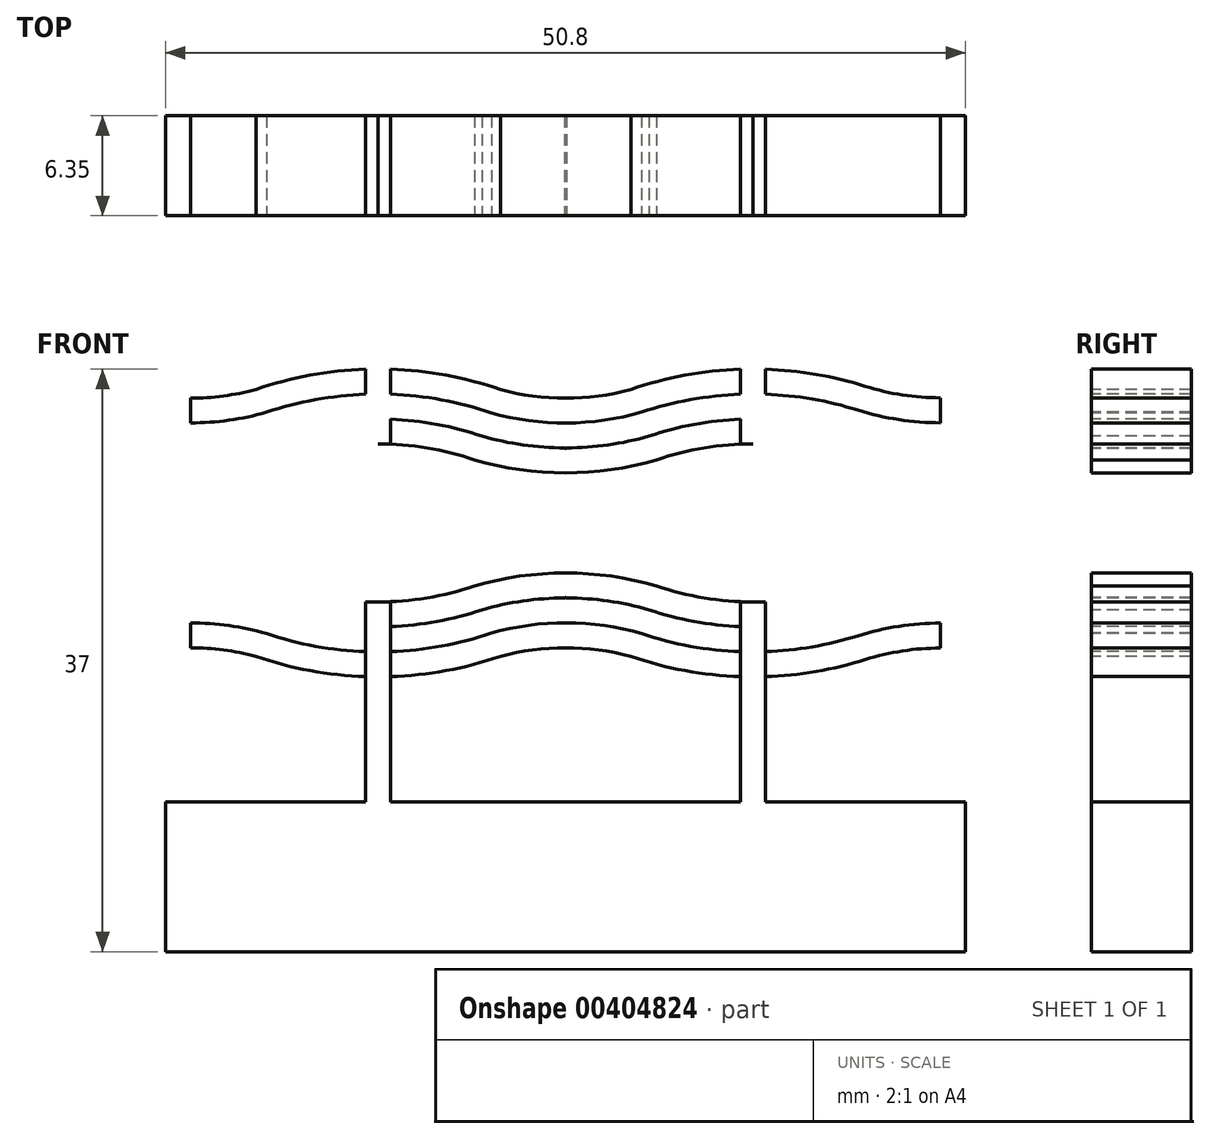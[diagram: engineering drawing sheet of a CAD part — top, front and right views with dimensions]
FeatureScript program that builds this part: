
annotation { "Feature Type Name" : "Feature", "Feature Type Description" : "" }
export const myFeature = defineFeature(function(context is Context, id is Id, definition is map)
    precondition{}
    {
        {
            var Q0;
            Q0=qCreatedBy(makeId("Front.planeOp"),FACE);
            var sketch = newSketch(context, id + "F0", { "sketchPlane" : qUnion([Q0])});
            skLineSegment(sketch, "E0.bottom", {"start": v(25.4, -4.76) * mm, "end": v(-25.4, -4.76) * mm});
            skLineSegment(sketch, "E0.top", {"start": v(25.4, 4.76) * mm, "end": v(-25.4, 4.76) * mm});
            skLineSegment(sketch, "E0.left", {"start": v(25.4, -4.76) * mm, "end": v(25.4, 4.76) * mm});
            skLineSegment(sketch, "E0.right", {"start": v(-25.4, -4.76) * mm, "end": v(-25.4, 4.76) * mm});
            skPoint(sketch, "E0.middle", {"position": v(0, 0) * mm});
            skLineSegment(sketch, "E1.bottom", {"start": v(-12.7, 4.76) * mm, "end": v(-11.11, 4.76) * mm});
            skLineSegment(sketch, "E1.top", {"start": v(-12.7, 17.46) * mm, "end": v(-11.11, 17.46) * mm});
            skLineSegment(sketch, "E1.left", {"start": v(-12.7, 4.76) * mm, "end": v(-12.7, 17.46) * mm});
            skLineSegment(sketch, "E1.right", {"start": v(-11.11, 4.76) * mm, "end": v(-11.11, 17.46) * mm});
            skLineSegment(sketch, "E2.bottom", {"start": v(11.11, 17.46) * mm, "end": v(12.7, 17.46) * mm});
            skLineSegment(sketch, "E2.top", {"start": v(11.11, 4.76) * mm, "end": v(12.7, 4.76) * mm});
            skLineSegment(sketch, "E2.left", {"start": v(12.7, 17.46) * mm, "end": v(12.7, 4.76) * mm});
            skLineSegment(sketch, "E2.right", {"start": v(11.11, 17.46) * mm, "end": v(11.11, 4.76) * mm});
            skSolve(sketch);
        }
        {
            var Q0;
            Q0 = qSketchRegion(id + "F0", true);
            extrude(context, id + "F1", {"entities" : qUnion([Q0]), "depth" : 6.35 * mm});
        }
        {
            var Q0;
            Q0=makeQuery(id+"F1.opExtrude","CAP_FACE",FACE,{"disambiguationData":[OSD([sQuery(id+"F0.wireOp",EDGE,"E0.bottom"),sQuery(id+"F0.wireOp",EDGE,"E0.top"),sQuery(id+"F0.wireOp",EDGE,"E0.left"),sQuery(id+"F0.wireOp",EDGE,"E0.right"),sQuery(id+"F0.wireOp",EDGE,"E1.top"),sQuery(id+"F0.wireOp",EDGE,"E1.left"),sQuery(id+"F0.wireOp",EDGE,"E1.right"),sQuery(id+"F0.wireOp",EDGE,"E2.bottom"),sQuery(id+"F0.wireOp",EDGE,"E2.left"),sQuery(id+"F0.wireOp",EDGE,"E2.right")])],"isStart":false});
            var sketch = newSketch(context, id + "F2", { "sketchPlane" : qUnion([Q0])});
            skArc(sketch, "E3", {"start": v(-18.03, 18.47) * mm, "mid": v(-11.9, 17.46) * mm, "end": v(-5.78, 18.47) * mm});
            skLineSegment(sketch, "E4", {"start": v(-11.9, 17.46) * mm, "end": v(-11.9, -4.76) * mm, "construction": true});
            skLineSegment(sketch, "E5", {"start": v(11.9, 17.46) * mm, "end": v(11.9, -4.76) * mm, "construction": true});
            skArc(sketch, "E6", {"start": v(5.78, 18.47) * mm, "mid": v(11.9, 17.46) * mm, "end": v(18.03, 18.47) * mm});
            skArc(sketch, "E7", {"start": v(-18.51, 16.96) * mm, "mid": v(-11.9, 15.88) * mm, "end": v(-5.3, 16.96) * mm});
            skArc(sketch, "E8", {"start": v(5.3, 16.96) * mm, "mid": v(11.9, 15.88) * mm, "end": v(18.51, 16.96) * mm});
            skArc(sketch, "E9", {"start": v(5.3, 16.96) * mm, "mid": v(0, 17.71) * mm, "end": v(-5.3, 16.96) * mm});
            skArc(sketch, "E10.trimOffspring", {"start": v(5.78, 18.47) * mm, "mid": v(0, 19.3) * mm, "end": v(-5.78, 18.47) * mm});
            skArc(sketch, "E11.MirrorCS", {"start": v(-23.81, 19.3) * mm, "mid": v(-20.9, 19.1) * mm, "end": v(-18.03, 18.47) * mm});
            skArc(sketch, "E12.MirrorCS", {"start": v(-23.81, 17.71) * mm, "mid": v(-21.13, 17.52) * mm, "end": v(-18.51, 16.96) * mm});
            skArc(sketch, "E13.MirrorCS", {"start": v(18.03, 18.47) * mm, "mid": v(20.9, 19.1) * mm, "end": v(23.81, 19.3) * mm});
            skArc(sketch, "E14.MirrorCS", {"start": v(18.51, 16.96) * mm, "mid": v(21.13, 17.52) * mm, "end": v(23.81, 17.71) * mm});
            skLineSegment(sketch, "E15", {"start": v(-23.81, 19.3) * mm, "end": v(-23.81, 17.71) * mm});
            skLineSegment(sketch, "E16", {"start": v(23.81, 19.3) * mm, "end": v(23.81, 17.71) * mm});
            skPoint(sketch, "E16.startSnap0", {"position": v(23.81, 19.3) * mm});
            skLineSegment(sketch, "E17", {"start": v(-25.4, 22.48) * mm, "end": v(25.4, 22.48) * mm, "construction": true});
            skArc(sketch, "E18.MirrorCS", {"start": v(-23.81, 25.65) * mm, "mid": v(-20.9, 25.86) * mm, "end": v(-18.03, 26.48) * mm});
            skArc(sketch, "E19.MirrorCS", {"start": v(-23.81, 27.24) * mm, "mid": v(-21.13, 27.43) * mm, "end": v(-18.51, 28) * mm});
            skArc(sketch, "E20.MirrorCS", {"start": v(-18.51, 28) * mm, "mid": v(-11.9, 29.08) * mm, "end": v(-5.3, 28) * mm});
            skArc(sketch, "E21.MirrorCS", {"start": v(-18.03, 26.48) * mm, "mid": v(-11.9, 27.49) * mm, "end": v(-5.78, 26.48) * mm});
            skArc(sketch, "E22.MirrorCS", {"start": v(5.78, 26.48) * mm, "mid": v(0, 25.65) * mm, "end": v(-5.78, 26.48) * mm});
            skArc(sketch, "E23.MirrorCS", {"start": v(5.3, 28) * mm, "mid": v(0, 27.24) * mm, "end": v(-5.3, 28) * mm});
            skArc(sketch, "E24.MirrorCS", {"start": v(5.78, 26.48) * mm, "mid": v(11.9, 27.49) * mm, "end": v(18.03, 26.48) * mm});
            skArc(sketch, "E25.MirrorCS", {"start": v(5.3, 28) * mm, "mid": v(11.9, 29.08) * mm, "end": v(18.51, 28) * mm});
            skArc(sketch, "E26.MirrorCS", {"start": v(18.03, 26.48) * mm, "mid": v(20.9, 25.86) * mm, "end": v(23.81, 25.65) * mm});
            skArc(sketch, "E27.MirrorCS", {"start": v(18.51, 28) * mm, "mid": v(21.13, 27.43) * mm, "end": v(23.81, 27.24) * mm});
            skLineSegment(sketch, "E28.MirrorCS", {"start": v(23.81, 25.65) * mm, "end": v(23.81, 27.24) * mm});
            skLineSegment(sketch, "E29", {"start": v(-23.81, 27.24) * mm, "end": v(-23.81, 25.65) * mm});
            skArc(sketch, "E30", {"start": v(-18.98, 15.44) * mm, "mid": v(-21.37, 15.95) * mm, "end": v(-23.81, 16.13) * mm});
            skArc(sketch, "E31", {"start": v(-23.81, 17.75) * mm, "mid": v(-23.79, 17.73) * mm, "end": v(-23.76, 17.71) * mm});
            skArc(sketch, "E32", {"start": v(0, 17.75) * mm, "mid": v(0.03, 17.73) * mm, "end": v(0.05, 17.71) * mm});
            skArc(sketch, "E33", {"start": v(23.81, 16.12) * mm, "mid": v(21.16, 15.91) * mm, "end": v(18.58, 15.31) * mm});
            skArc(sketch, "E34.trimOffspring", {"start": v(-18.98, 15.44) * mm, "mid": v(-11.84, 14.29) * mm, "end": v(-4.7, 15.49) * mm});
            skArc(sketch, "E35.trimOffspring", {"start": v(-0.05, 17.71) * mm, "mid": v(-0.03, 17.73) * mm, "end": v(0, 17.75) * mm});
            skArc(sketch, "E36.trimOffspring", {"start": v(4.83, 15.44) * mm, "mid": v(11.7, 14.29) * mm, "end": v(18.58, 15.31) * mm});
            skArc(sketch, "E37.trimOffspring", {"start": v(4.83, 15.44) * mm, "mid": v(0.07, 16.13) * mm, "end": v(-4.7, 15.49) * mm});
            skArc(sketch, "E38.trimOffspring", {"start": v(23.76, 17.71) * mm, "mid": v(23.79, 17.73) * mm, "end": v(23.81, 17.75) * mm});
            skLineSegment(sketch, "E39", {"start": v(-23.81, 19.3) * mm, "end": v(-23.81, 4.76) * mm});
            skLineSegment(sketch, "E40", {"start": v(23.81, 17.75) * mm, "end": v(23.81, 4.76) * mm});
            skArc(sketch, "E41", {"start": v(-19.67, 14) * mm, "mid": v(-11.9, 12.7) * mm, "end": v(-4.14, 14) * mm});
            skArc(sketch, "E42", {"start": v(11.92, 9.17) * mm, "mid": v(11.91, 9.17) * mm, "end": v(11.9, 9.18) * mm});
            skArc(sketch, "E43", {"start": v(23.81, 14.53) * mm, "mid": v(21.4, 14.34) * mm, "end": v(19.05, 13.8) * mm});
            skArc(sketch, "E44.trimOffspring", {"start": v(-19.67, 14) * mm, "mid": v(-21.72, 14.41) * mm, "end": v(-23.81, 14.55) * mm});
            skArc(sketch, "E45.trimOffspring", {"start": v(0.4, 16.12) * mm, "mid": v(1.46, 16.8) * mm, "end": v(2.5, 17.55) * mm});
            skArc(sketch, "E46.trimOffspring", {"start": v(11.92, 9.17) * mm, "mid": v(11.91, 9.16) * mm, "end": v(11.9, 9.15) * mm});
            skArc(sketch, "E47.trimOffspring", {"start": v(4.14, 14) * mm, "mid": v(11.58, 12.7) * mm, "end": v(19.05, 13.8) * mm});
            skArc(sketch, "E48.trimOffspring", {"start": v(4.14, 14) * mm, "mid": v(0, 14.55) * mm, "end": v(-4.14, 14) * mm});
            skSolve(sketch);
        }
        {
            var Q0;
            {var subQ6=sQuery(id+"F2.wireOp",EDGE,"E11.MirrorCS");Q0=makeQuery(id+"F2.imprint","IMPRINT",FACE,{"disambiguationData":[TD([[makeQuery(id+"F2.imprint","IMPRINT",EDGE,{"derivedFrom":subQ6}),-1.0]])]});}
            var Q1;
            {var subQ5=sQuery(id+"F2.wireOp",EDGE,"E30");Q1=makeQuery(id+"F2.imprint","IMPRINT",FACE,{"disambiguationData":[TD([[makeQuery(id+"F2.imprint","IMPRINT",EDGE,{"derivedFrom":subQ5}),1.0]])]});}
            var Q2;
            {var subQ5=sQuery(id+"F2.wireOp",EDGE,"E10.trimOffspring");Q2=makeQuery(id+"F2.imprint","IMPRINT",FACE,{"disambiguationData":[TD([[makeQuery(id+"F2.imprint","IMPRINT",EDGE,{"derivedFrom":subQ5}),1.0]])]});}
            var Q3;
            {var subQ12=sQuery(id+"F2.wireOp",EDGE,"E48.trimOffspring");Q3=makeQuery(id+"F2.imprint","IMPRINT",FACE,{"disambiguationData":[TD([[makeQuery(id+"F2.imprint","IMPRINT",EDGE,{"derivedFrom":subQ12}),-1.0]])]});}
            var Q4;
            {var subQ6=sQuery(id+"F2.wireOp",EDGE,"E13.MirrorCS");Q4=makeQuery(id+"F2.imprint","IMPRINT",FACE,{"disambiguationData":[TD([[makeQuery(id+"F2.imprint","IMPRINT",EDGE,{"derivedFrom":subQ6}),-1.0]])]});}
            var Q5;
            {var subQ2=sQuery(id+"F2.wireOp",EDGE,"E33");Q5=makeQuery(id+"F2.imprint","IMPRINT",FACE,{"disambiguationData":[TD([[makeQuery(id+"F2.imprint","IMPRINT",EDGE,{"derivedFrom":subQ2}),1.0]])]});}
            extrude(context, id + "F3", {"entities" : qUnion([Q0, Q1, Q2, Q3, Q4, Q5]), "oppositeDirection" : true, "depth" : 6.35 * mm});
        }
        {
            var Q0;
            Q0=makeQuery(id+"F1.opExtrude","SWEPT_FACE",FACE,{"disambiguationData":[OSD([sQuery(id+"F0.wireOp",EDGE,"E0.bottom")])]});
            cPlane(context, id + "F4", {"entities" : qUnion([Q0]), "cplaneType" : CPlaneType.OFFSET, "offset" : 27.24 * mm, "oppositeDirection" : true, "width" : 152.4 * mm, "height" : 152.4 * mm});
        }
        {
            var Q0;
            Q0=makeQuery(id+"F3.opExtrude","SWEPT_BODY",BODY,{"disambiguationData":[OSD([sQuery(id+"F0.wireOp",EDGE,"E1.left"),sQuery(id+"F2.wireOp",EDGE,"E30"),sQuery(id+"F2.wireOp",EDGE,"E34.trimOffspring"),sQuery(id+"F2.wireOp",EDGE,"E39"),sQuery(id+"F2.wireOp",EDGE,"E41"),sQuery(id+"F2.wireOp",EDGE,"E44.trimOffspring")])]});
            var Q1;
            Q1=makeQuery(id+"F3.opExtrude","SWEPT_BODY",BODY,{"disambiguationData":[OSD([sQuery(id+"F0.wireOp",EDGE,"E1.top"),sQuery(id+"F0.wireOp",EDGE,"E1.left"),sQuery(id+"F2.wireOp",EDGE,"E3"),sQuery(id+"F2.wireOp",EDGE,"E7"),sQuery(id+"F2.wireOp",EDGE,"E11.MirrorCS"),sQuery(id+"F2.wireOp",EDGE,"E12.MirrorCS"),sQuery(id+"F2.wireOp",EDGE,"E31"),sQuery(id+"F2.wireOp",EDGE,"E39")])]});
            var Q2;
            Q2=makeQuery(id+"F3.opExtrude","SWEPT_BODY",BODY,{"disambiguationData":[OSD([sQuery(id+"F0.wireOp",EDGE,"E1.right"),sQuery(id+"F0.wireOp",EDGE,"E2.right"),sQuery(id+"F2.wireOp",EDGE,"E34.trimOffspring"),sQuery(id+"F2.wireOp",EDGE,"E36.trimOffspring"),sQuery(id+"F2.wireOp",EDGE,"E37.trimOffspring"),sQuery(id+"F2.wireOp",EDGE,"E41"),sQuery(id+"F2.wireOp",EDGE,"E47.trimOffspring"),sQuery(id+"F2.wireOp",EDGE,"E48.trimOffspring")])]});
            var Q3;
            Q3=makeQuery(id+"F3.opExtrude","SWEPT_BODY",BODY,{"disambiguationData":[OSD([sQuery(id+"F0.wireOp",EDGE,"E1.top"),sQuery(id+"F0.wireOp",EDGE,"E1.right"),sQuery(id+"F0.wireOp",EDGE,"E2.bottom"),sQuery(id+"F0.wireOp",EDGE,"E2.right"),sQuery(id+"F2.wireOp",EDGE,"E3"),sQuery(id+"F2.wireOp",EDGE,"E6"),sQuery(id+"F2.wireOp",EDGE,"E7"),sQuery(id+"F2.wireOp",EDGE,"E8"),sQuery(id+"F2.wireOp",EDGE,"E9"),sQuery(id+"F2.wireOp",EDGE,"E10.trimOffspring"),sQuery(id+"F2.wireOp",EDGE,"E32"),sQuery(id+"F2.wireOp",EDGE,"E35.trimOffspring")])]});
            var Q4;
            Q4=makeQuery(id+"F3.opExtrude","SWEPT_BODY",BODY,{"disambiguationData":[OSD([sQuery(id+"F0.wireOp",EDGE,"E2.bottom"),sQuery(id+"F0.wireOp",EDGE,"E2.left"),sQuery(id+"F2.wireOp",EDGE,"E6"),sQuery(id+"F2.wireOp",EDGE,"E8"),sQuery(id+"F2.wireOp",EDGE,"E13.MirrorCS"),sQuery(id+"F2.wireOp",EDGE,"E14.MirrorCS"),sQuery(id+"F2.wireOp",EDGE,"E16"),sQuery(id+"F2.wireOp",EDGE,"E38.trimOffspring")])]});
            var Q5;
            Q5=makeQuery(id+"F3.opExtrude","SWEPT_BODY",BODY,{"disambiguationData":[OSD([sQuery(id+"F0.wireOp",EDGE,"E2.left"),sQuery(id+"F2.wireOp",EDGE,"E33"),sQuery(id+"F2.wireOp",EDGE,"E36.trimOffspring"),sQuery(id+"F2.wireOp",EDGE,"E40"),sQuery(id+"F2.wireOp",EDGE,"E43"),sQuery(id+"F2.wireOp",EDGE,"E47.trimOffspring")])]});
            var Q6;
            Q6=qCreatedBy(id+"F4.planeOp",FACE);
            mirror(context, id + "F5", {"entities" : qUnion([Q0, Q1, Q2, Q3, Q4, Q5]), "mirrorPlane" : qUnion([Q6])});
        }
    });
